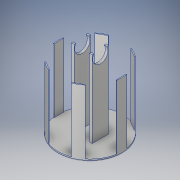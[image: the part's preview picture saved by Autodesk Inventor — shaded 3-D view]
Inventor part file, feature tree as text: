
AUTODESK INVENTOR PART (.ipt)
format: ipt  version: 2018 (Build 220112000, 112)  size: 179,200 bytes
history: native  units: in
note: dims shown in document units (in); Inventor stores cm internally (conversion verified against a paired STEP export)
features: extrude x4, sketch x4, fillet x1
ambient origin geometry x8: Origin, YZ Plane, XZ Plane, XY Plane, X Axis, Y Axis, Z Axis, Center Point
bodies: Solid1 (feature_tree)
feature tree (9):
  extrude  "Extrusion1"  Depth=0.013in TaperAngle=0.0deg
  extrude  "Extrusion2"  Depth=0.312in TaperAngle=360.0deg
  fillet  "Fillet1"  Radius=0.312in
  extrude  "Extrusion3"  Depth=0.013in
  extrude  "Extrusion4"  Depth=0.075in
  sketch  "Sketch1"  dims[d0=0.314in d1=0.013in d2=0.0in]
  sketch  "Sketch2"  dims[d3=90.0deg d4=2.3622in d6=360.0deg d8=0.312in d9=0.0in]
  sketch  "Sketch3"  dims[d10=0.0075in d11=0.013in]
  sketch  "Sketch5"  dims[d12=0.08in d13=0.04in d14=0.0375in d15=0.375in d16=0.0in d18=0.075in d19=0.35in d20=0.0in]
